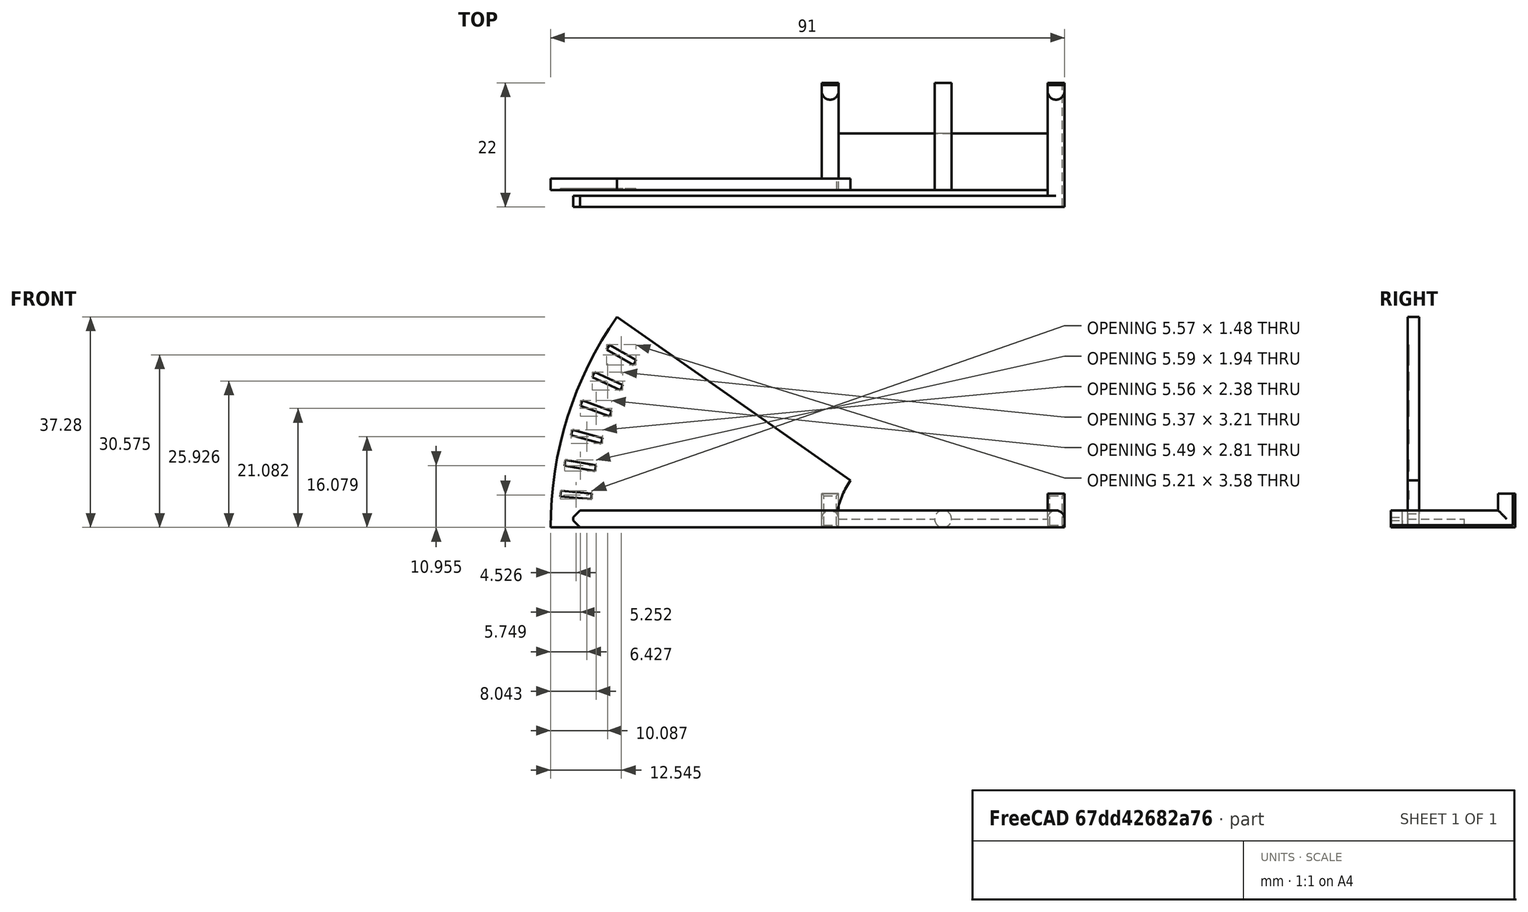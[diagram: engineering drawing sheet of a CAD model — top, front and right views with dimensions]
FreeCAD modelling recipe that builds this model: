
FCSTD DOCUMENT  (FreeCAD 0.18R16146 (Git))
Label: belt-tesioner-meter
License: All rights reserved
LicenseURL: http://en.wikipedia.org/wiki/All_rights_reserved
objects: Part::Box×12, Part::Cylinder×8, Part::Cut×3, Part::MultiFuse×2, Part::Chamfer×2, Mesh::Feature×1, Part::Fillet×1, Part::Feature×1
note: 29 computed .brp shape members not serialized (recipe doc carries the construction recipe); baked Part::Feature solids carry a one-line shape summary decoded from their .brp

FEATURE [Mesh::Feature] belt
  Placement = pos=(-127.5,-93.9,0) rot=(0,0,1;0rad)
FEATURE [Part::Cylinder] Cylinder
  Angle = 35
  AttacherType = Attacher::AttachEngine3D
  Height = 2
  Placement = pos=(17,3,-7e-16) rot=(0,0.707107,0.707107;3.14159rad)
  Radius = 65
FEATURE [Part::Cylinder] Cylinder001
  Angle = 360
  AttacherType = Attacher::AttachEngine3D
  Height = 2
  Placement = pos=(17,3,-1e-15) rot=(-1,0,0;1.5708rad)
  Radius = 14.5
FEATURE [Part::Cut] Cut
  Base = -> Cylinder
  Tool = -> Cylinder001
FEATURE [Part::Box] Box  label="Cube"
  AttacherType = Attacher::AttachEngine3D
  Height = 3
  Length = 87
  Placement = pos=(-44,0,0) rot=(0,0,1;0rad)
  Width = 2
FEATURE [Part::Cylinder] Cylinder002
  Angle = 360
  AttacherType = Attacher::AttachEngine3D
  Height = 19
  Placement = pos=(1.5,3,1.5) rot=(1,0,0;4.71239rad)
  Radius = 1.5
FEATURE [Part::Cylinder] Cylinder003
  Angle = 360
  AttacherType = Attacher::AttachEngine3D
  Height = 4.5
  Placement = pos=(1.5,20.5,1.5) rot=(0,0,1;0rad)
  Radius = 1.5
FEATURE [Part::Cylinder] Cylinder004
  Angle = 360
  AttacherType = Attacher::AttachEngine3D
  Height = 19
  Placement = pos=(21.5,3,1.5) rot=(-1,0,0;1.5708rad)
  Radius = 1.5
FEATURE [Part::Cylinder] Cylinder005
  Angle = 360
  AttacherType = Attacher::AttachEngine3D
  Height = 22
  Placement = pos=(41.5,0,1.5) rot=(-1,0,0;1.5708rad)
  Radius = 1.5
FEATURE [Part::Cylinder] Cylinder006
  Angle = 360
  AttacherType = Attacher::AttachEngine3D
  Height = 4.5
  Placement = pos=(41.5,20.5,1.5) rot=(0,0,1;0rad)
  Radius = 1.5
FEATURE [Part::Box] Box001  label="Cube001"
  AttacherType = Attacher::AttachEngine3D
  Height = 1.5
  Length = 43
  Placement = pos=(0,3,0) rot=(0,0,1;0rad)
  Width = 10
FEATURE [Part::Box] Box002  label="Cube002"
  AttacherType = Attacher::AttachEngine3D
  Height = 1.5
  Length = 3
  Placement = pos=(40,2,0) rot=(0,0,1;0rad)
  Width = 20
FEATURE [Part::Box] Box003  label="Cube003"
  AttacherType = Attacher::AttachEngine3D
  Height = 1.5
  Length = 3
  Placement = pos=(0,3,0) rot=(0,0,1;0rad)
  Width = 19
FEATURE [Part::Box] Box004  label="Cube004"
  AttacherType = Attacher::AttachEngine3D
  Height = 6
  Length = 3
  Placement = pos=(0,20.5,0) rot=(0,0,1;0rad)
  Width = 1.5
FEATURE [Part::Box] Box005  label="Cube005"
  AttacherType = Attacher::AttachEngine3D
  Height = 6
  Length = 3
  Placement = pos=(40,20.5,0) rot=(0,0,1;0rad)
  Width = 1.5
FEATURE [Part::Cylinder] Cylinder007
  Angle = 360
  AttacherType = Attacher::AttachEngine3D
  Height = 15
  Placement = pos=(17,3,-1e-15) rot=(1,0,0;4.71239rad)
  Radius = 58
FEATURE [Part::Box] Box007  label="Cube007"
  AttacherType = Attacher::AttachEngine3D
  Height = 63
  Length = 1
  Placement = pos=(16.5,3,0) rot=(0,1,0;4.79965rad)
  Width = 0.5
FEATURE [Part::Box] Box008  label="Cube008"
  AttacherType = Attacher::AttachEngine3D
  Height = 63
  Length = 1
  Placement = pos=(16.5,3,0) rot=(0,-1,0;1.39626rad)
  Width = 0.5
FEATURE [Part::Box] Box009  label="Cube009"
  AttacherType = Attacher::AttachEngine3D
  Height = 63
  Length = 1
  Placement = pos=(16.5,3,0) rot=(0,-1,0;1.309rad)
  Width = 0.5
FEATURE [Part::Box] Box010  label="Cube010"
  AttacherType = Attacher::AttachEngine3D
  Height = 63
  Length = 1
  Placement = pos=(16.5,3,0) rot=(0,-1,0;1.22173rad)
  Width = 0.5
FEATURE [Part::Box] Box011  label="Cube011"
  AttacherType = Attacher::AttachEngine3D
  Height = 63
  Length = 1
  Placement = pos=(16.5,3,0) rot=(0,-1,0;1.13446rad)
  Width = 0.5
FEATURE [Part::Box] Box012  label="Cube012"
  AttacherType = Attacher::AttachEngine3D
  Height = 63
  Length = 1
  Placement = pos=(16.5,3,0) rot=(0,-1,0;1.0472rad)
  Width = 0.5
FEATURE [Part::MultiFuse] Fusion
  Shapes = -> [Box012,Box011,Box010,Box009,Box008,Box007]
FEATURE [Part::Cut] Cut001
  Base = -> Fusion
  Placement = pos=(0,-0.25,0) rot=(0,0,1;0rad)
  Tool = -> Cylinder007
FEATURE [Part::Cut] Cut002
  Base = -> Cut
  Tool = -> Cut001
FEATURE [Part::Chamfer] Chamfer
  Base = -> Box
  Edges = 2 edges r=1.2: [Edge2,Edge4]
FEATURE [Part::Fillet] Fillet
  Base = -> Chamfer
  Edges = 1 edges r=1.5: [Edge18]
FEATURE [Part::MultiFuse] Fusion001
  Shapes = -> [Fillet,Cylinder002,Cylinder006,Box005,Cylinder005,Box004,Cylinder004,Box003,Cylinder003,Box001,Box002,Cut002]
FEATURE [Part::Feature] Fusion001001  label="Fusion002"
  shape: bbox 91 x 22 x 37.28 mm, 61 faces (baked)
FEATURE [Part::Chamfer] Chamfer001
  Base = -> Fusion001001
  Edges = 9 edges r=0.4: [Edge39,Edge41,Edge42,Edge43,Edge47,Edge48,Edge60,Edge62,Edge63]
